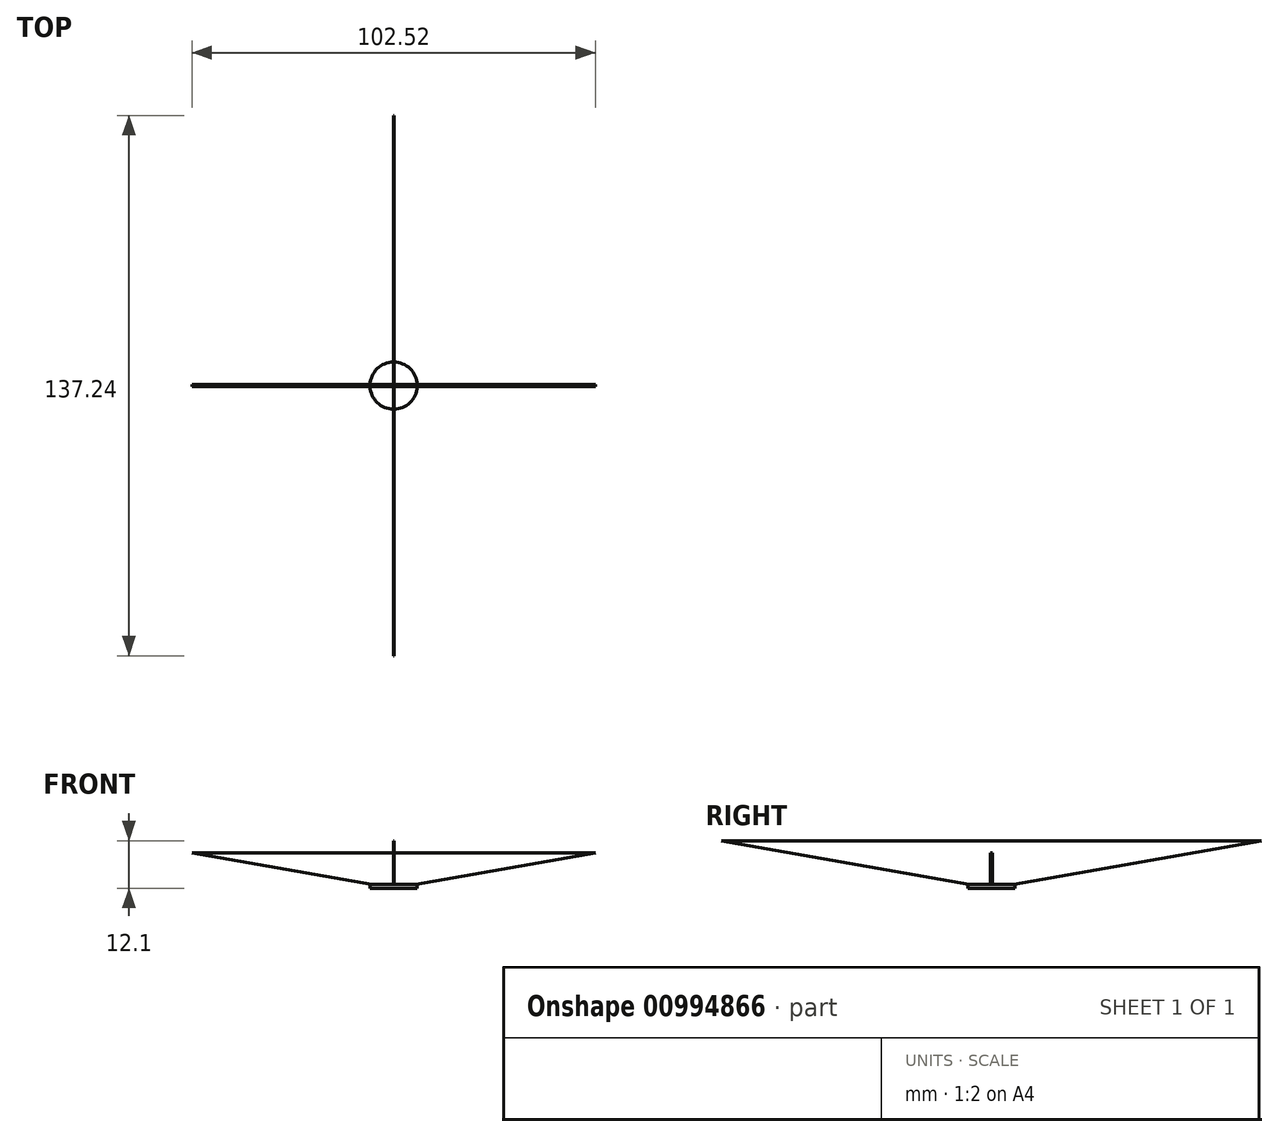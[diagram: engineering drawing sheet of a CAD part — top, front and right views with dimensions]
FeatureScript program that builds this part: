
annotation { "Feature Type Name" : "Feature", "Feature Type Description" : "" }
export const myFeature = defineFeature(function(context is Context, id is Id, definition is map)
    precondition{}
    {
        {
            var Q0;
            Q0=qCreatedBy(makeId("Top.planeOp"),FACE);
            var sketch = newSketch(context, id + "F0", { "sketchPlane" : qUnion([Q0])});
            skCircle(sketch, "E0", {"center": v(0, 0) * mm, "radius": 6 * mm});
            skSolve(sketch);
        }
        {
            var Q0;
            Q0=makeQuery(id+"F0.imprint","IMPRINT",FACE,{"disambiguationData":[TD([[makeQuery(id+"F0.imprint","IMPRINT",EDGE,{"derivedFrom":sQuery(id+"F0.wireOp",EDGE,"E0")}),1.0]])]});
            extrude(context, id + "F1", {"entities" : qUnion([Q0]), "depth" : 1 * mm, "offsetDistance" : 25 * mm});
        }
        {
            var Q0;
            Q0=qCreatedBy(makeId("Right.planeOp"),FACE);
            var sketch = newSketch(context, id + "F2", { "sketchPlane" : qUnion([Q0])});
            skLineSegment(sketch, "E1", {"start": v(0, 0) * mm, "end": v(68.62, 12.1) * mm});
            skLineSegment(sketch, "E2", {"start": v(0, 0) * mm, "end": v(-68.62, 12.1) * mm});
            skLineSegment(sketch, "E3", {"start": v(68.62, 12.1) * mm, "end": v(68.62, 0) * mm, "construction": true});
            skLineSegment(sketch, "E4", {"start": v(-68.62, 12.1) * mm, "end": v(-68.62, 0) * mm, "construction": true});
            skLineSegment(sketch, "E5", {"start": v(68.62, 12.1) * mm, "end": v(-68.62, 12.1) * mm});
            skSolve(sketch);
        }
        {
            var Q0;
            Q0 = qSketchRegion(id + "F2", true);
            extrude(context, id + "F3", {"entities" : qUnion([Q0]), "operationType" : NewBodyOperationType.ADD, "endBound" : BoundingType.SYMMETRIC, "depth" : .1 * mm, "offsetDistance" : 25 * mm});
        }
        {
            var Q0;
            Q0=qCreatedBy(makeId("Front.planeOp"),FACE);
            var sketch = newSketch(context, id + "F4", { "sketchPlane" : qUnion([Q0])});
            skLineSegment(sketch, "E6", {"start": v(0, 0) * mm, "end": v(51.26, 9.04) * mm});
            skLineSegment(sketch, "E7", {"start": v(0, 0) * mm, "end": v(-51.26, 9.04) * mm});
            skLineSegment(sketch, "E8", {"start": v(51.26, 9.04) * mm, "end": v(51.26, 0) * mm, "construction": true});
            skLineSegment(sketch, "E9", {"start": v(-51.26, 9.04) * mm, "end": v(-51.26, 0) * mm, "construction": true});
            skLineSegment(sketch, "E10", {"start": v(51.26, 9.04) * mm, "end": v(-51.26, 9.04) * mm});
            skSolve(sketch);
        }
        {
            var Q0;
            Q0=makeQuery(id+"F4.imprint","IMPRINT",FACE,{"disambiguationData":[TD([[makeQuery(id+"F4.imprint","IMPRINT",EDGE,{"derivedFrom":sQuery(id+"F4.wireOp",EDGE,"E6")}),1.0]])]});
            extrude(context, id + "F5", {"entities" : qUnion([Q0]), "operationType" : NewBodyOperationType.ADD, "endBound" : BoundingType.SYMMETRIC, "depth" : .5 * mm, "offsetDistance" : 25 * mm});
        }
    });
